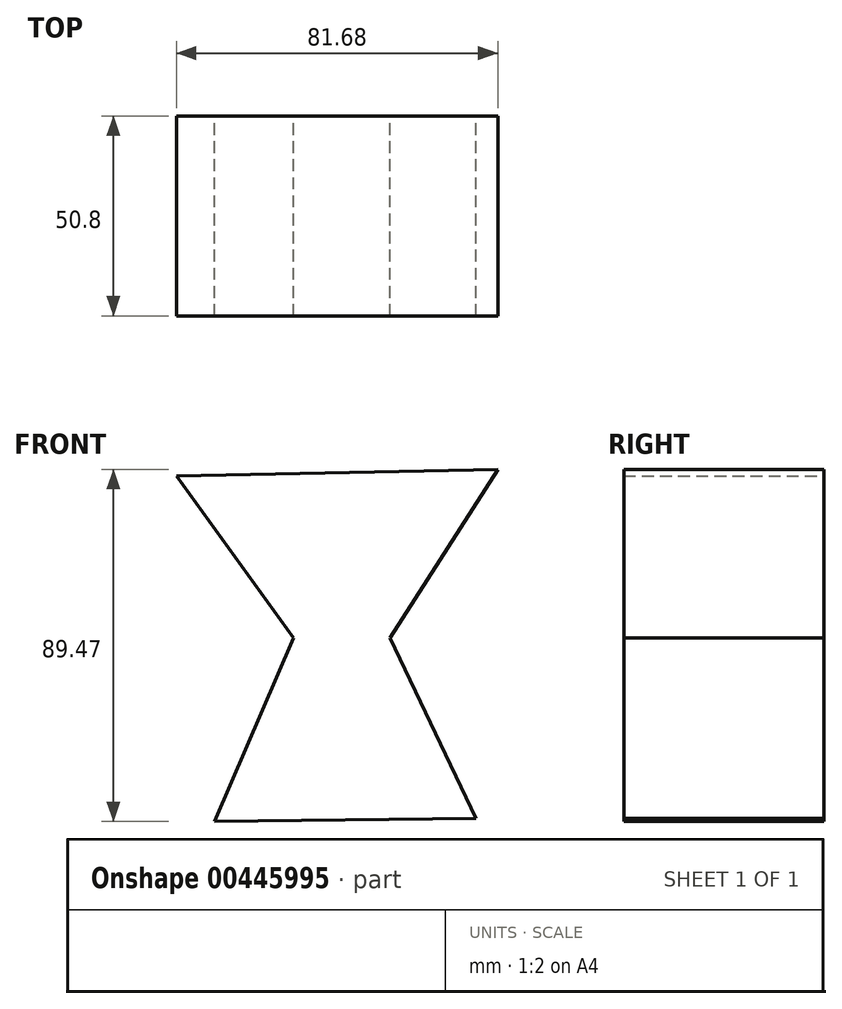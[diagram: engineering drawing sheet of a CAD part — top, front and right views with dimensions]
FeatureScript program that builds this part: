
annotation { "Feature Type Name" : "Feature", "Feature Type Description" : "" }
export const myFeature = defineFeature(function(context is Context, id is Id, definition is map)
    precondition{}
    {
        {
            var Q0;
            Q0=qCreatedBy(makeId("Front.planeOp"),FACE);
            var sketch = newSketch(context, id + "F0", { "sketchPlane" : qUnion([Q0])});
            skLineSegment(sketch, "E0", {"start": v(-9.02, 0) * mm, "end": v(-38.8, 41.16) * mm});
            skLineSegment(sketch, "E1", {"start": v(-9.02, 0) * mm, "end": v(-29.07, -46.68) * mm});
            skLineSegment(sketch, "E2", {"start": v(15.5, 0) * mm, "end": v(42.87, 42.79) * mm});
            skLineSegment(sketch, "E3", {"start": v(42.87, 42.79) * mm, "end": v(-38.8, 41.16) * mm});
            skLineSegment(sketch, "E4", {"start": v(15.5, 0) * mm, "end": v(37.27, -45.9) * mm});
            skLineSegment(sketch, "E5", {"start": v(37.27, -45.9) * mm, "end": v(-29.07, -46.68) * mm});
            skSolve(sketch);
        }
        {
            var Q0;
            Q0=makeQuery(id+"F0.imprint","IMPRINT",FACE,{"disambiguationData":[TD([[makeQuery(id+"F0.imprint","IMPRINT",EDGE,{"derivedFrom":sQuery(id+"F0.wireOp",EDGE,"E0")}),-1.0]])]});
            extrude(context, id + "F1", {"entities" : qUnion([Q0]), "depth" : 50.8 * mm});
        }
    });
